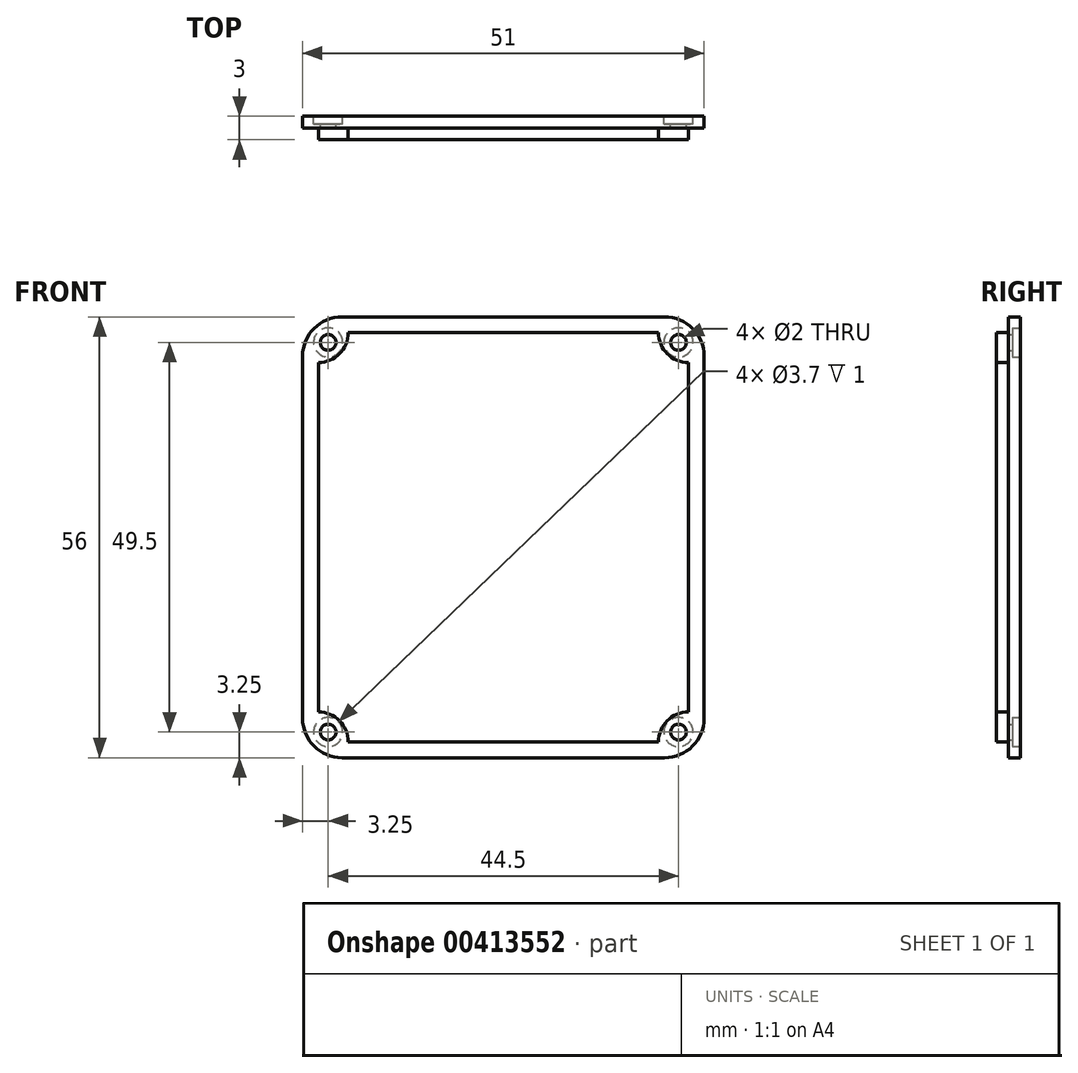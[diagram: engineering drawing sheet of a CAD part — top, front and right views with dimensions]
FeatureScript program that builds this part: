
annotation { "Feature Type Name" : "Feature", "Feature Type Description" : "" }
export const myFeature = defineFeature(function(context is Context, id is Id, definition is map)
    precondition{}
    {
        {
            var Q0;
            Q0=qCreatedBy(makeId("Front.planeOp"),FACE);
            var sketch = newSketch(context, id + "F0", { "sketchPlane" : qUnion([Q0])});
            skLineSegment(sketch, "E0.bottom", {"start": v(0, 0) * mm, "end": v(51, 0) * mm});
            skLineSegment(sketch, "E0.top", {"start": v(0, 56) * mm, "end": v(51, 56) * mm});
            skLineSegment(sketch, "E0.left", {"start": v(0, 0) * mm, "end": v(0, 56) * mm});
            skLineSegment(sketch, "E0.right", {"start": v(51, 0) * mm, "end": v(51, 56) * mm});
            skLineSegment(sketch, "E1.0", {"start": v(2, 2) * mm, "end": v(2, 54) * mm});
            skLineSegment(sketch, "E1.1", {"start": v(2, 2) * mm, "end": v(49, 2) * mm});
            skLineSegment(sketch, "E1.2", {"start": v(49, 2) * mm, "end": v(49, 54) * mm});
            skLineSegment(sketch, "E1.3", {"start": v(2, 54) * mm, "end": v(49, 54) * mm});
            skLineSegment(sketch, "E2", {"start": v(25.5, 63.65) * mm, "end": v(25.5, -8.7) * mm, "construction": true});
            skPoint(sketch, "E2.startSnap0", {"position": v(25.5, 56) * mm});
            skLineSegment(sketch, "E3", {"start": v(-6.03, 28) * mm, "end": v(65.3, 28) * mm, "construction": true});
            skPoint(sketch, "E3.startSnap0", {"position": v(0, 28) * mm});
            skPoint(sketch, "E3.endSnap0", {"position": v(51, 28) * mm});
            skSolve(sketch);
        }
        {
            var Q0;
            Q0=makeQuery(id+"F0.imprint","IMPRINT",FACE,{"disambiguationData":[TD([[makeQuery(id+"F0.imprint","IMPRINT",EDGE,{"derivedFrom":sQuery(id+"F0.wireOp",EDGE,"E0.bottom")}),1.0]])]});
            var Q1;
            Q1=makeQuery(id+"F0.imprint","IMPRINT",FACE,{"disambiguationData":[TD([[makeQuery(id+"F0.imprint","IMPRINT",EDGE,{"derivedFrom":sQuery(id+"F0.wireOp",EDGE,"E1.0")}),-1.0]])]});
            extrude(context, id + "F1", {"entities" : qUnion([Q0, Q1]), "depth" : 1.5 * mm});
        }
        {
            var Q0;
            Q0=makeQuery(id+"F1.opExtrude","SWEPT_EDGE",EDGE,{"disambiguationData":[OSD([sQuery(id+"F0.wireOp",EDGE,"E0.top"),sQuery(id+"F0.wireOp",EDGE,"E0.left")])]});
            var Q1;
            Q1=makeQuery(id+"F1.opExtrude","SWEPT_EDGE",EDGE,{"disambiguationData":[OSD([sQuery(id+"F0.wireOp",EDGE,"E0.top"),sQuery(id+"F0.wireOp",EDGE,"E0.right")])]});
            var Q2;
            Q2=makeQuery(id+"F1.opExtrude","SWEPT_EDGE",EDGE,{"disambiguationData":[OSD([sQuery(id+"F0.wireOp",EDGE,"E0.bottom"),sQuery(id+"F0.wireOp",EDGE,"E0.right")])]});
            var Q3;
            Q3=makeQuery(id+"F1.opExtrude","SWEPT_EDGE",EDGE,{"disambiguationData":[OSD([sQuery(id+"F0.wireOp",EDGE,"E0.bottom"),sQuery(id+"F0.wireOp",EDGE,"E0.left")])]});
            fillet(context, id + "F2", {"entities" : qUnion([Q0, Q1, Q2, Q3]), "radius" : 5 * mm, "tangentPropagation" : true, "allowEdgeOverflow" : false});
        }
        {
            var Q0;
            Q0=makeQuery(id+"F0.imprint","IMPRINT",FACE,{"disambiguationData":[TD([[makeQuery(id+"F0.imprint","IMPRINT",EDGE,{"derivedFrom":sQuery(id+"F0.wireOp",EDGE,"E1.0")}),-1.0]])]});
            extrude(context, id + "F3", {"entities" : qUnion([Q0]), "operationType" : NewBodyOperationType.ADD, "depth" : 3 * mm});
        }
        {
            var Q0;
            Q0=makeQuery(id+"F0.imprint","IMPRINT",FACE,{"disambiguationData":[TD([[makeQuery(id+"F0.imprint","IMPRINT",EDGE,{"derivedFrom":sQuery(id+"F0.wireOp",EDGE,"E1.0")}),-1.0]])]});
            var sketch = newSketch(context, id + "F4", { "sketchPlane" : qUnion([Q0])});
            skPoint(sketch, "E4", {"position": v(47.75, 52.75) * mm});
            skPoint(sketch, "E5.MirrorP", {"position": v(3.25, 52.75) * mm});
            skPoint(sketch, "E6.MirrorP", {"position": v(3.25, 3.25) * mm});
            skPoint(sketch, "E7.MirrorP", {"position": v(47.75, 3.25) * mm});
            skSolve(sketch);
        }
        {
            var Q0;
            Q0=sQuery(id+"F4.wireOp",VERTEX,"E4");
            var Q1;
            Q1=sQuery(id+"F4.wireOp",VERTEX,"E5.MirrorP");
            var Q2;
            Q2=sQuery(id+"F4.wireOp",VERTEX,"E7.MirrorP");
            var Q3;
            Q3=sQuery(id+"F4.wireOp",VERTEX,"E6.MirrorP");
            var Q4;
            Q4=makeQuery(id+"F1.opExtrude","SWEPT_BODY",BODY,{"disambiguationData":[OSD([sQuery(id+"F0.wireOp",EDGE,"E0.bottom"),sQuery(id+"F0.wireOp",EDGE,"E0.top"),sQuery(id+"F0.wireOp",EDGE,"E0.left"),sQuery(id+"F0.wireOp",EDGE,"E0.right")])]});
            hole(context, id + "F5", {"style" : HoleStyle.C_BORE, "endStyle" : HoleEndStyle.THROUGH, "oppositeDirection" : true, "holeDiameter" : 2 * mm, "cBoreDiameter" : 3.7 * mm, "cBoreDepth" : 1 * mm, "isTappedThrough" : true, "tappedDepth" : 12 * mm, "tapClearance" : 3, "startFromSketch" : true, "locations" : qUnion([Q0, Q1, Q2, Q3]), "scope" : qUnion([Q4])});
        }
        {
            var Q0;
            Q0=makeQuery(id+"F3.opExtrude","CAP_FACE",FACE,{"disambiguationData":[OSD([sQuery(id+"F0.wireOp",EDGE,"E1.0"),sQuery(id+"F0.wireOp",EDGE,"E1.1"),sQuery(id+"F0.wireOp",EDGE,"E1.2"),sQuery(id+"F0.wireOp",EDGE,"E1.3")])],"isStart":false});
            var sketch = newSketch(context, id + "F6", { "sketchPlane" : qUnion([Q0])});
            skArc(sketch, "E8", {"start": v(2, 50.2) * mm, "mid": v(4.69, 51.31) * mm, "end": v(5.8, 54) * mm});
            skLineSegment(sketch, "E9", {"start": v(5.8, 54) * mm, "end": v(2, 54) * mm});
            skLineSegment(sketch, "E10", {"start": v(2, 54) * mm, "end": v(2, 50.2) * mm});
            skArc(sketch, "E11.MirrorCS", {"start": v(49, 50.2) * mm, "mid": v(46.31, 51.31) * mm, "end": v(45.2, 54) * mm});
            skLineSegment(sketch, "E12.MirrorCS", {"start": v(49, 54) * mm, "end": v(49, 50.2) * mm});
            skLineSegment(sketch, "E13.MirrorCS", {"start": v(45.2, 54) * mm, "end": v(49, 54) * mm});
            skArc(sketch, "E14.MirrorCS", {"start": v(49, 5.8) * mm, "mid": v(46.31, 4.69) * mm, "end": v(45.2, 2) * mm});
            skLineSegment(sketch, "E15.MirrorCS", {"start": v(45.2, 2) * mm, "end": v(49, 2) * mm});
            skLineSegment(sketch, "E16.MirrorCS", {"start": v(49, 2) * mm, "end": v(49, 5.8) * mm});
            skArc(sketch, "E17.MirrorCS", {"start": v(2, 5.8) * mm, "mid": v(4.69, 4.69) * mm, "end": v(5.8, 2) * mm});
            skLineSegment(sketch, "E18.MirrorCS", {"start": v(2, 2) * mm, "end": v(2, 5.8) * mm});
            skLineSegment(sketch, "E19.MirrorCS", {"start": v(5.8, 2) * mm, "end": v(2, 2) * mm});
            skSolve(sketch);
        }
        {
            var Q0;
            Q0 = qSketchRegion(id + "F6", true);
            extrude(context, id + "F7", {"entities" : qUnion([Q0]), "operationType" : NewBodyOperationType.REMOVE, "oppositeDirection" : true, "depth" : 1.5 * mm});
        }
    });
